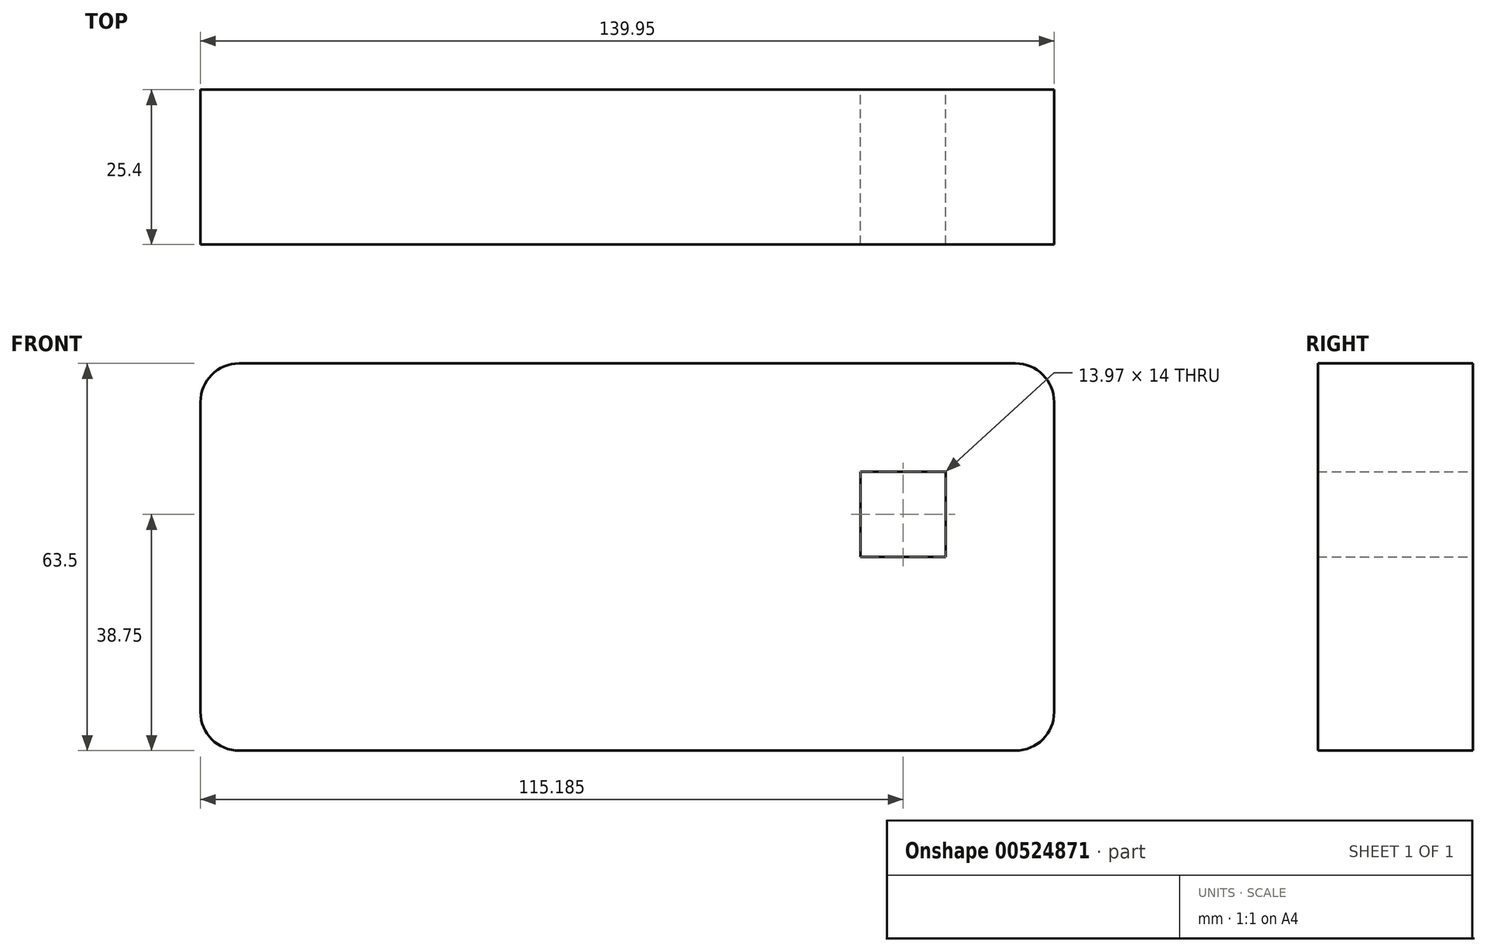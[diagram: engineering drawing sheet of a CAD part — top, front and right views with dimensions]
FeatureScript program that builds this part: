
annotation { "Feature Type Name" : "Feature", "Feature Type Description" : "" }
export const myFeature = defineFeature(function(context is Context, id is Id, definition is map)
    precondition{}
    {
        {
            var Q0;
            Q0=qCreatedBy(makeId("Front.planeOp"),FACE);
            var sketch = newSketch(context, id + "F0", { "sketchPlane" : qUnion([Q0])});
            skLineSegment(sketch, "E0.bottom", {"start": v(-6.35, 0) * mm, "end": v(-133.6, 0) * mm});
            skLineSegment(sketch, "E0.top", {"start": v(-6.35, 63.5) * mm, "end": v(-133.6, 63.5) * mm});
            skLineSegment(sketch, "E0.left", {"start": v(0, 6.35) * mm, "end": v(0, 57.15) * mm});
            skLineSegment(sketch, "E0.right", {"start": v(-139.95, 6.35) * mm, "end": v(-139.95, 57.15) * mm});
            skPoint(sketch, "E1.visualSharp", {"position": v(-139.95, 0) * mm});
            skArc(sketch, "E1.filletArc", {"start": v(-139.95, 6.35) * mm, "mid": v(-138.1, 1.86) * mm, "end": v(-133.6, 0) * mm});
            skPoint(sketch, "E2.visualSharp", {"position": v(-139.95, 63.5) * mm});
            skArc(sketch, "E2.filletArc", {"start": v(-133.6, 63.5) * mm, "mid": v(-138.1, 61.64) * mm, "end": v(-139.95, 57.15) * mm});
            skPoint(sketch, "E3.visualSharp", {"position": v(0, 63.5) * mm});
            skArc(sketch, "E3.filletArc", {"start": v(0, 57.15) * mm, "mid": v(-1.86, 61.64) * mm, "end": v(-6.35, 63.5) * mm});
            skPoint(sketch, "E4.visualSharp", {"position": v(0, 0) * mm});
            skArc(sketch, "E4.filletArc", {"start": v(-6.35, 0) * mm, "mid": v(-1.86, 1.86) * mm, "end": v(0, 6.35) * mm});
            skLineSegment(sketch, "E5", {"start": v(0, 31.75) * mm, "end": v(-17.78, 31.75) * mm, "construction": true});
            skLineSegment(sketch, "E6", {"start": v(-17.78, 31.75) * mm, "end": v(-17.78, 0) * mm, "construction": true});
            skLineSegment(sketch, "E7.bottom", {"start": v(-17.78, 31.75) * mm, "end": v(-31.75, 31.75) * mm});
            skLineSegment(sketch, "E7.top", {"start": v(-17.78, 45.75) * mm, "end": v(-31.75, 45.75) * mm});
            skLineSegment(sketch, "E7.left", {"start": v(-17.78, 31.75) * mm, "end": v(-17.78, 45.75) * mm});
            skLineSegment(sketch, "E7.right", {"start": v(-31.75, 31.75) * mm, "end": v(-31.75, 45.75) * mm});
            skLineSegment(sketch, "E8", {"start": v(-23.03, 63.5) * mm, "end": v(-23.03, 48.51) * mm, "construction": true});
            skSolve(sketch);
        }
        {
            var Q0;
            Q0 = qSketchRegion(id + "F0", true);
            extrude(context, id + "F1", {"entities" : qUnion([Q0]), "depth" : 25.4 * mm, "offsetDistance" : 25.4 * mm});
        }
    });
